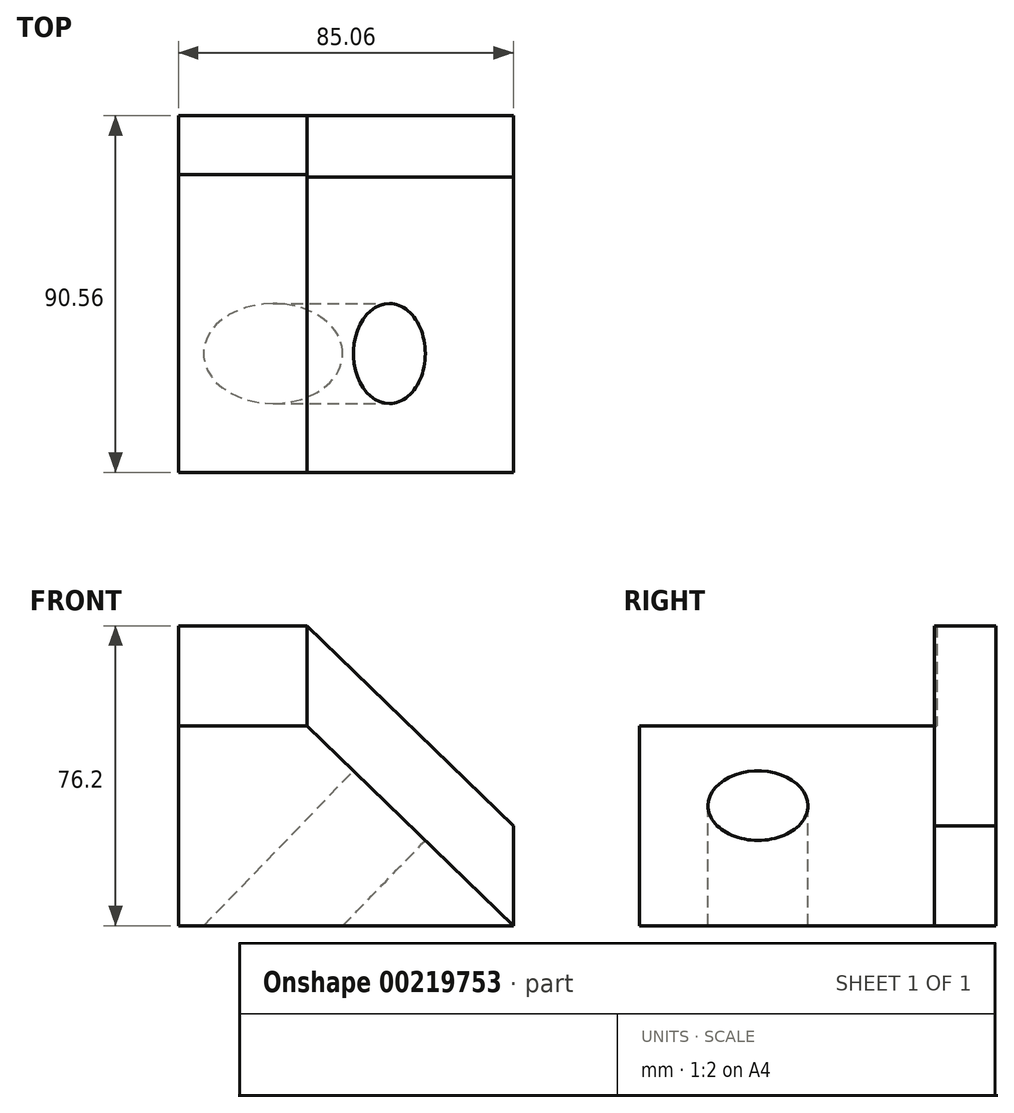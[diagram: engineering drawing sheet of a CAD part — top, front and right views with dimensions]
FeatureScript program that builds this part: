
annotation { "Feature Type Name" : "Feature", "Feature Type Description" : "" }
export const myFeature = defineFeature(function(context is Context, id is Id, definition is map)
    precondition{}
    {
        {
            var Q0;
            Q0=qCreatedBy(makeId("Top.planeOp"),FACE);
            var sketch = newSketch(context, id + "F0", { "sketchPlane" : qUnion([Q0])});
            skLineSegment(sketch, "E0.bottom", {"start": v(42.53, -45.28) * mm, "end": v(-42.53, -45.28) * mm});
            skLineSegment(sketch, "E0.top", {"start": v(42.53, 45.28) * mm, "end": v(-42.53, 45.28) * mm});
            skLineSegment(sketch, "E0.left", {"start": v(42.53, -45.28) * mm, "end": v(42.53, 45.28) * mm});
            skLineSegment(sketch, "E0.right", {"start": v(-42.53, -45.28) * mm, "end": v(-42.53, 45.28) * mm});
            skPoint(sketch, "E0.middle", {"position": v(0, 0) * mm});
            skSolve(sketch);
        }
        {
            var Q0;
            Q0=makeQuery(id+"F0.imprint","IMPRINT",FACE,{"disambiguationData":[TD([[makeQuery(id+"F0.imprint","IMPRINT",EDGE,{"derivedFrom":sQuery(id+"F0.wireOp",EDGE,"E0.bottom")}),-1.0]])]});
            extrude(context, id + "F1", {"entities" : qUnion([Q0]), "depth" : 50.8 * mm});
        }
        {
            var Q0;
            Q0=makeQuery(id+"F1.opExtrude","SWEPT_FACE",FACE,{"disambiguationData":[OSD([sQuery(id+"F0.wireOp",EDGE,"E0.bottom")])]});
            var sketch = newSketch(context, id + "F2", { "sketchPlane" : qUnion([Q0])});
            skLineSegment(sketch, "E1.0", {"start": v(42.53, 50.8) * mm, "end": v(-42.53, 50.8) * mm});
            skLineSegment(sketch, "E2.0", {"start": v(42.53, 50.8) * mm, "end": v(42.53, 0) * mm});
            skLineSegment(sketch, "E3", {"start": v(-9.9, 50.8) * mm, "end": v(42.53, 0) * mm});
            skSolve(sketch);
        }
        {
            var Q0;
            Q0 = qSketchRegion(id + "F2", true);
            extrude(context, id + "F3", {"entities" : qUnion([Q0]), "operationType" : NewBodyOperationType.REMOVE, "endBound" : BoundingType.THROUGH_ALL, "oppositeDirection" : true, "depth" : 25.4 * mm});
        }
        {
            var Q0;
            Q0=makeQuery(id+"F3.boolean.opBoolean","COPY",FACE,{"derivedFrom":makeQuery(id+"F3.opExtrude","SWEPT_FACE",FACE,{"disambiguationData":[OSD([sQuery(id+"F2.wireOp",EDGE,"E3")])]})});
            var sketch = newSketch(context, id + "F4", { "sketchPlane" : qUnion([Q0])});
            skEllipse(sketch, "E4", {"center": v(-13.28, -15.12) * mm, "majorRadius": 11.69 * mm, "minorRadius": 12.86 * mm, "majorAxis": v(1, 0)});
            skSolve(sketch);
        }
        {
            var Q0;
            Q0=sQuery(id+"F4.wireOp",VERTEX,"E4.center");
            var Q1;
            Q1=makeQuery(id+"F1.opExtrude","SWEPT_BODY",BODY,{"disambiguationData":[OSD([sQuery(id+"F0.wireOp",EDGE,"E0.bottom"),sQuery(id+"F0.wireOp",EDGE,"E0.top"),sQuery(id+"F0.wireOp",EDGE,"E0.left"),sQuery(id+"F0.wireOp",EDGE,"E0.right")])]});
            hole(context, id + "F5", {"style" : HoleStyle.SIMPLE, "endStyle" : HoleEndStyle.THROUGH, "holeDiameter" : 25.4 * mm, "locations" : qUnion([Q0]), "scope" : qUnion([Q1]), "isTappedThrough" : true});
        }
        {
            var Q0;
            Q0=makeQuery(id+"F3.boolean.opBoolean","COPY",FACE,{"derivedFrom":makeQuery(id+"F3.opExtrude","SWEPT_FACE",FACE,{"disambiguationData":[OSD([sQuery(id+"F2.wireOp",EDGE,"E3")])]})});
            var sketch = newSketch(context, id + "F6", { "sketchPlane" : qUnion([Q0])});
            skLineSegment(sketch, "E5.0", {"start": v(-42.46, 45.28) * mm, "end": v(30.55, 45.28) * mm});
            skLineSegment(sketch, "E6.0", {"start": v(30.55, -45.28) * mm, "end": v(30.55, 45.28) * mm});
            skLineSegment(sketch, "E7", {"start": v(30.55, 29.73) * mm, "end": v(-42.46, 29.73) * mm});
            skSolve(sketch);
        }
        {
            var Q0;
            Q0=makeQuery(id+"F1.opExtrude","CAP_FACE",FACE,{"disambiguationData":[OSD([sQuery(id+"F0.wireOp",EDGE,"E0.bottom"),sQuery(id+"F0.wireOp",EDGE,"E0.top"),sQuery(id+"F0.wireOp",EDGE,"E0.left"),sQuery(id+"F0.wireOp",EDGE,"E0.right")])],"isStart":false});
            var sketch = newSketch(context, id + "F7", { "sketchPlane" : qUnion([Q0])});
            skLineSegment(sketch, "E8.0", {"start": v(-9.9, 45.28) * mm, "end": v(-42.53, 45.28) * mm});
            skLineSegment(sketch, "E9.0", {"start": v(-42.53, -45.28) * mm, "end": v(-42.53, 45.28) * mm});
            skLineSegment(sketch, "E10", {"start": v(-9.9, 30.32) * mm, "end": v(-42.53, 30.32) * mm});
            skSolve(sketch);
        }
        {
            var Q0;
            Q0 = qSketchRegion(id + "F7", true);
            var Q1;
            {var subQ0=sQuery(id+"F7.wireOp",EDGE,"E8.0");Q1=makeQuery(id+"F7.imprint","IMPRINT",FACE,{"disambiguationData":[TD([[makeQuery(id+"F7.imprint","IMPRINT",EDGE,{"derivedFrom":subQ0}),1.0]])]});}
            var Q2;
            {var subQ0=sQuery(id+"F6.wireOp",EDGE,"E5.0");Q2=makeQuery(id+"F6.imprint","IMPRINT",FACE,{"disambiguationData":[TD([[makeQuery(id+"F6.imprint","IMPRINT",EDGE,{"derivedFrom":subQ0}),-1.0]])]});}
            extrude(context, id + "F8", {"entities" : qUnion([Q0, Q1, Q2]), "operationType" : NewBodyOperationType.ADD, "depth" : 25.4 * mm});
        }
    });
